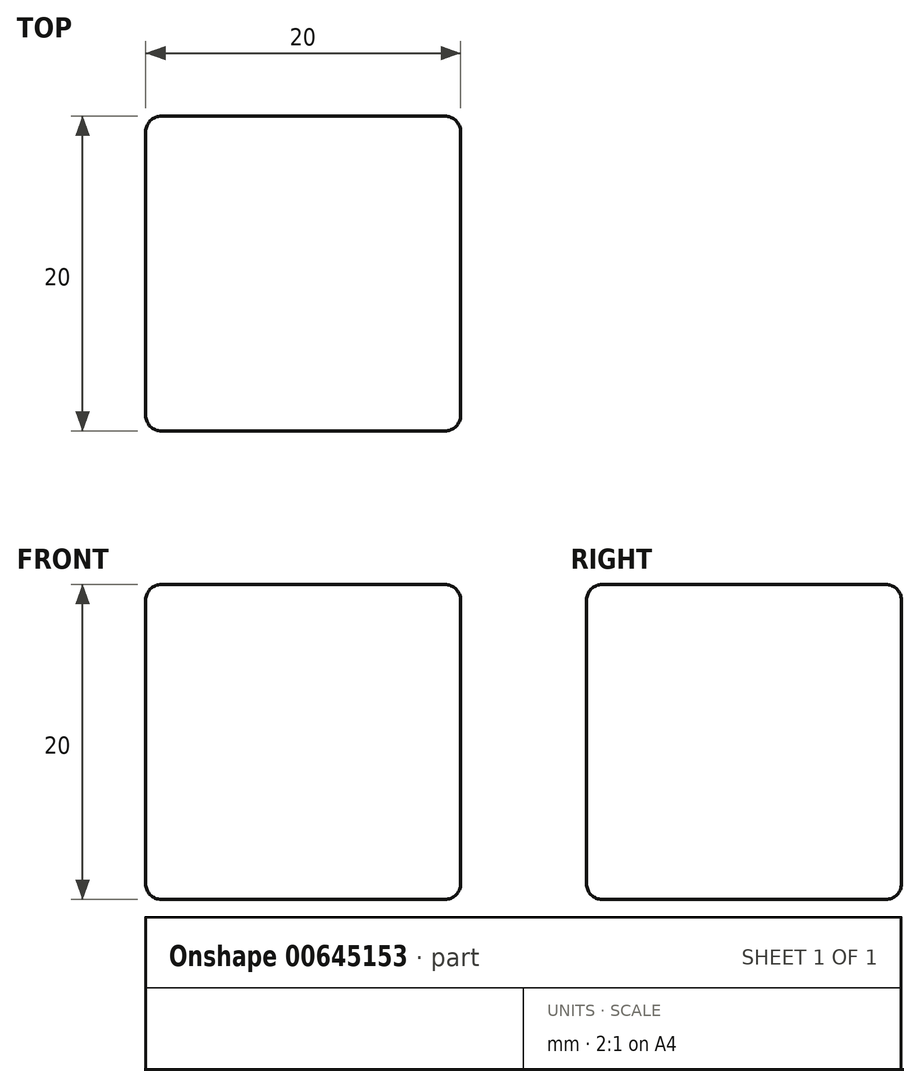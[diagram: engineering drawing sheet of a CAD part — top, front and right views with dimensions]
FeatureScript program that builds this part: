
annotation { "Feature Type Name" : "Feature", "Feature Type Description" : "" }
export const myFeature = defineFeature(function(context is Context, id is Id, definition is map)
    precondition{}
    {
        {
            var Q0;
            Q0=qCreatedBy(makeId("Top.planeOp"),FACE);
            var sketch = newSketch(context, id + "F0", { "sketchPlane" : qUnion([Q0])});
            skLineSegment(sketch, "E0.bottom", {"start": v(0, 0) * mm, "end": v(-20, 0) * mm});
            skLineSegment(sketch, "E0.top", {"start": v(0, 20) * mm, "end": v(-20, 20) * mm});
            skLineSegment(sketch, "E0.left", {"start": v(0, 0) * mm, "end": v(0, 20) * mm});
            skLineSegment(sketch, "E0.right", {"start": v(-20, 0) * mm, "end": v(-20, 20) * mm});
            skSolve(sketch);
        }
        {
            var Q0;
            Q0=makeQuery(id+"F0.imprint","IMPRINT",FACE,{"disambiguationData":[TD([[makeQuery(id+"F0.imprint","IMPRINT",EDGE,{"derivedFrom":sQuery(id+"F0.wireOp",EDGE,"E0.bottom")}),-1.0]])]});
            extrude(context, id + "F1", {"entities" : qUnion([Q0]), "depth" : 20 * mm, "offsetDistance" : 25 * mm});
        }
        {
            var Q0;
            Q0=makeQuery(id+"F1.opExtrude","CAP_EDGE",EDGE,{"disambiguationData":[OSD([sQuery(id+"F0.wireOp",EDGE,"E0.top")])],"isStart":false});
            var Q1;
            Q1=makeQuery(id+"F1.opExtrude","CAP_EDGE",EDGE,{"disambiguationData":[OSD([sQuery(id+"F0.wireOp",EDGE,"E0.left")])],"isStart":false});
            var Q2;
            Q2=makeQuery(id+"F1.opExtrude","SWEPT_EDGE",EDGE,{"disambiguationData":[OSD([sQuery(id+"F0.wireOp",EDGE,"E0.top"),sQuery(id+"F0.wireOp",EDGE,"E0.left")])]});
            var Q3;
            Q3=makeQuery(id+"F1.opExtrude","CAP_EDGE",EDGE,{"disambiguationData":[OSD([sQuery(id+"F0.wireOp",EDGE,"E0.left")])],"isStart":true});
            var Q4;
            Q4=makeQuery(id+"F1.opExtrude","CAP_EDGE",EDGE,{"disambiguationData":[OSD([sQuery(id+"F0.wireOp",EDGE,"E0.bottom")])],"isStart":false});
            var Q5;
            Q5=makeQuery(id+"F1.opExtrude","SWEPT_EDGE",EDGE,{"disambiguationData":[OSD([sQuery(id+"F0.wireOp",EDGE,"E0.top"),sQuery(id+"F0.wireOp",EDGE,"E0.right")])]});
            var Q6;
            Q6=makeQuery(id+"F1.opExtrude","CAP_EDGE",EDGE,{"disambiguationData":[OSD([sQuery(id+"F0.wireOp",EDGE,"E0.right")])],"isStart":false});
            var Q7;
            Q7=makeQuery(id+"F1.opExtrude","CAP_EDGE",EDGE,{"disambiguationData":[OSD([sQuery(id+"F0.wireOp",EDGE,"E0.top")])],"isStart":true});
            var Q8;
            Q8=makeQuery(id+"F1.opExtrude","CAP_EDGE",EDGE,{"disambiguationData":[OSD([sQuery(id+"F0.wireOp",EDGE,"E0.bottom")])],"isStart":true});
            var Q9;
            Q9=makeQuery(id+"F1.opExtrude","CAP_EDGE",EDGE,{"disambiguationData":[OSD([sQuery(id+"F0.wireOp",EDGE,"E0.right")])],"isStart":true});
            var Q10;
            Q10=makeQuery(id+"F1.opExtrude","SWEPT_EDGE",EDGE,{"disambiguationData":[OSD([sQuery(id+"F0.wireOp",EDGE,"E0.bottom"),sQuery(id+"F0.wireOp",EDGE,"E0.right")])]});
            var Q11;
            Q11=makeQuery(id+"F1.opExtrude","SWEPT_FACE",FACE,{"disambiguationData":[OSD([sQuery(id+"F0.wireOp",EDGE,"E0.left")])]});
            var Q12;
            Q12=makeQuery(id+"F1.opExtrude","SWEPT_EDGE",EDGE,{"disambiguationData":[OSD([sQuery(id+"F0.wireOp",EDGE,"E0.bottom"),sQuery(id+"F0.wireOp",EDGE,"E0.left")])]});
            fillet(context, id + "F2", {"entities" : qUnion([Q0, Q1, Q2, Q3, Q4, Q5, Q6, Q7, Q8, Q9, Q10, Q11, Q12]), "radius" : 1 * mm, "tangentPropagation" : true, "allowEdgeOverflow" : false});
        }
    });
